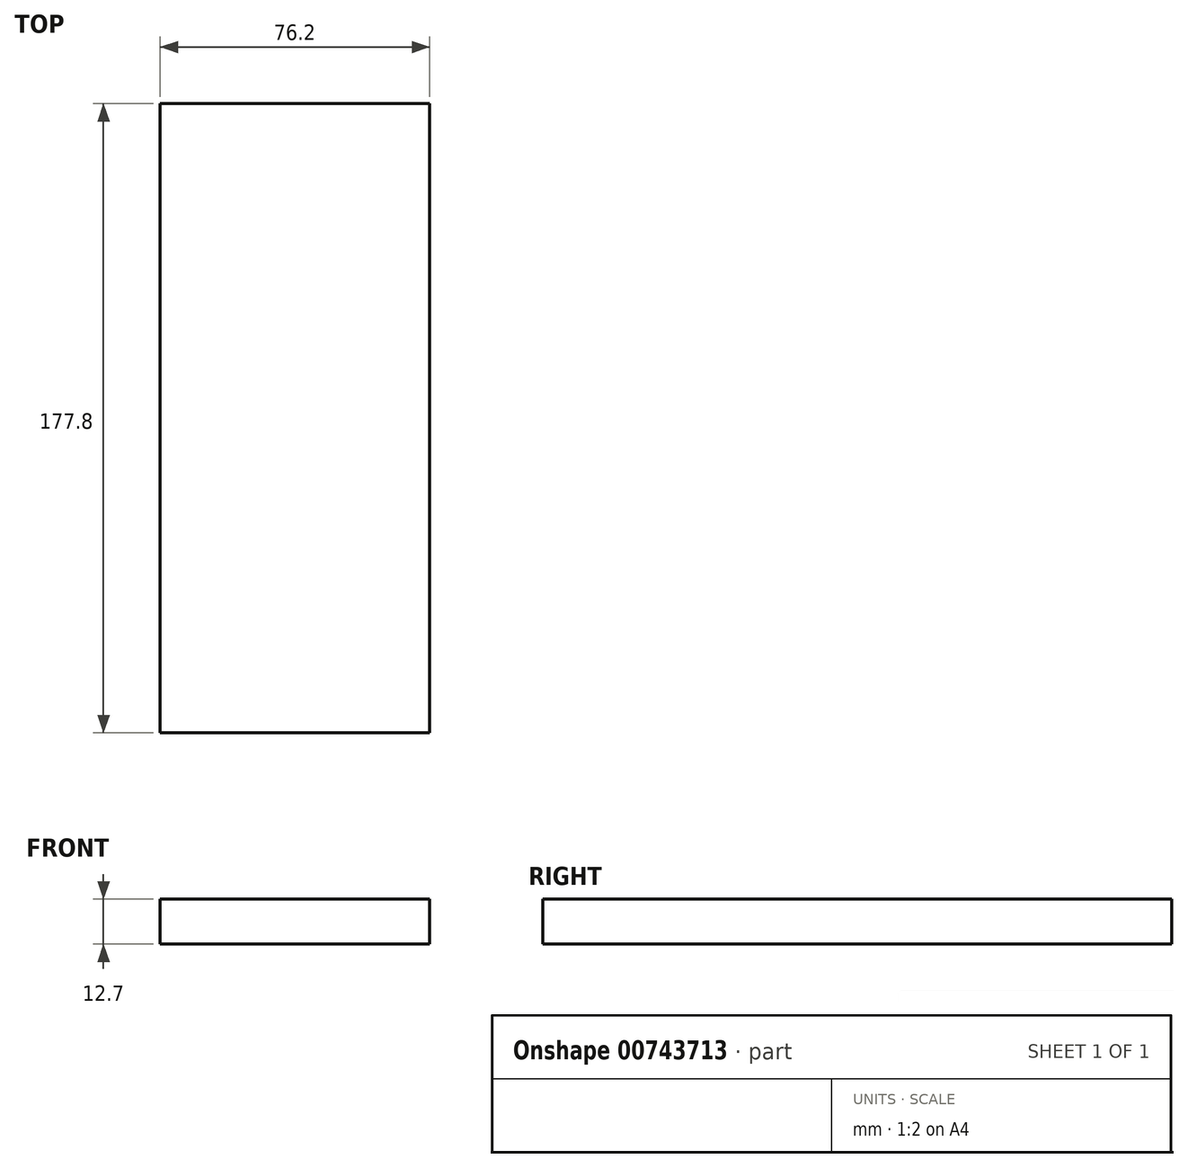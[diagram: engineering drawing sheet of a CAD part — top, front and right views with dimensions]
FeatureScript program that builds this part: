
annotation { "Feature Type Name" : "Feature", "Feature Type Description" : "" }
export const myFeature = defineFeature(function(context is Context, id is Id, definition is map)
    precondition{}
    {
        {
            var Q0;
            Q0=qCreatedBy(makeId("Top.planeOp"),FACE);
            var sketch = newSketch(context, id + "F0", { "sketchPlane" : qUnion([Q0])});
            skLineSegment(sketch, "E0.bottom", {"start": v(-38.82, 79.67) * mm, "end": v(37.38, 79.67) * mm});
            skLineSegment(sketch, "E0.top", {"start": v(-38.82, -98.13) * mm, "end": v(37.38, -98.13) * mm});
            skLineSegment(sketch, "E0.left", {"start": v(-38.82, 79.67) * mm, "end": v(-38.82, -98.13) * mm});
            skLineSegment(sketch, "E0.right", {"start": v(37.38, 79.67) * mm, "end": v(37.38, -98.13) * mm});
            skSolve(sketch);
        }
        {
            var Q0;
            Q0=makeQuery(id+"F0.imprint","IMPRINT",FACE,{"disambiguationData":[TD([[makeQuery(id+"F0.imprint","IMPRINT",EDGE,{"derivedFrom":sQuery(id+"F0.wireOp",EDGE,"E0.bottom")}),-1.0]])]});
            extrude(context, id + "F1", {"entities" : qUnion([Q0]), "depth" : 12.7 * mm, "offsetDistance" : 25.4 * mm});
        }
    });
